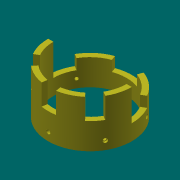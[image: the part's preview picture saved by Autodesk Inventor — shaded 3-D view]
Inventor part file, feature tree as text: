
AUTODESK INVENTOR PART (.ipt)
format: ipt  version: 2013 (Build 170138000, 138)  size: 282,624 bytes
history: native  units: mm
features: sketch x16, extrude x14, other x2, hole x2, pattern_circular x1
ambient origin geometry x8: Origin, YZ Plane, XZ Plane, XY Plane, X Axis, Y Axis, Z Axis, Center Point
feature tree (35):
  other  "ソリッド1"
  extrude  "押し出し1"  Depth=90.0mm
  extrude  "押し出し2"  Depth=80.0mm
  extrude  "押し出し3"  Depth=5.0mm TaperAngle=0.0deg
  extrude  "押し出し4"  Depth=80.0mm
  extrude  "押し出し5"  Depth=100.0mm TaperAngle=0.0deg
  extrude  "押し出し6"  Depth=70.0mm
  extrude  "押し出し7"  Depth=100.0mm TaperAngle=0.0deg
  extrude  "押し出し8"  Depth=55.0mm
  extrude  "押し出し9"  Depth=5.0mm TaperAngle=0.0deg
  hole  "穴1"  [1 undecoded]
  extrude  "押し出し10"  Depth=40.0mm TaperAngle=0.0deg
  extrude  "押し出し11"  Depth=13.962634mm
  other  "作業平面1"
  hole  "穴2"  [1 undecoded]
  pattern_circular  "円形状パターン1"  Angle=150.0deg  [1 undecoded]
  extrude  "押し出し12"  Depth=11.34464mm
  extrude  "押し出し13"  TaperAngle=30.0deg  [1 undecoded]
  extrude  "押し出し14"  Depth=40.0mm TaperAngle=0.0deg
  sketch  "スケッチ1"
  sketch  "スケッチ2"
  sketch  "スケッチ3"
  sketch  "スケッチ4"
  sketch  "スケッチ5"
  sketch  "スケッチ6"
  sketch  "スケッチ7"
  sketch  "スケッチ8"
  sketch  "スケッチ9"
  sketch  "スケッチ10"
  sketch  "スケッチ11"
  sketch  "スケッチ12"
  sketch  "スケッチ13"
  sketch  "スケッチ14"
  sketch  "スケッチ15"
  sketch  "スケッチ16"
note: 4 required parameter values undecoded (feature->parameter linkage not recoverable at this tier; creation-order binding heuristic only, values carry confidence <= 0.55)
